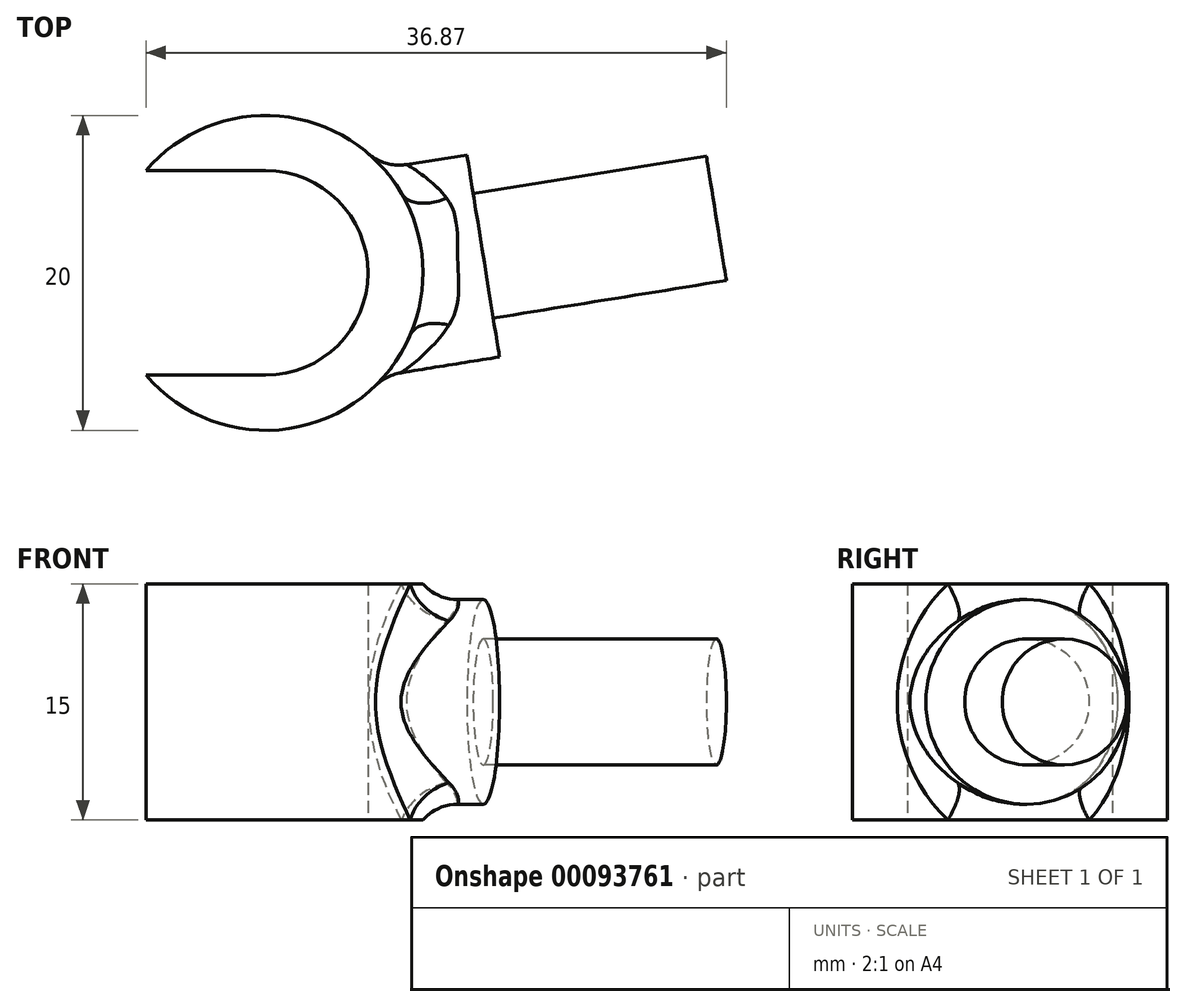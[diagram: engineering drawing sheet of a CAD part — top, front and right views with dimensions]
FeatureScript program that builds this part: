
annotation { "Feature Type Name" : "Feature", "Feature Type Description" : "" }
export const myFeature = defineFeature(function(context is Context, id is Id, definition is map)
    precondition{}
    {
        {
            var Q0;
            Q0=qCreatedBy(makeId("Top.planeOp"),FACE);
            var sketch = newSketch(context, id + "F0", { "sketchPlane" : qUnion([Q0])});
            skArc(sketch, "E0", {"start": v(-7.6, -6.5) * mm, "mid": v(10, 0) * mm, "end": v(-7.6, 6.5) * mm});
            skArc(sketch, "E1", {"start": v(0, -6.5) * mm, "mid": v(6.5, 0) * mm, "end": v(0, 6.5) * mm});
            skLineSegment(sketch, "E2", {"start": v(0, 6.5) * mm, "end": v(-7.6, 6.5) * mm});
            skLineSegment(sketch, "E3", {"start": v(0, -6.5) * mm, "end": v(-7.6, -6.5) * mm});
            skSolve(sketch);
        }
        {
            var Q0;
            Q0=makeQuery(id+"F0.imprint","IMPRINT",FACE,{"disambiguationData":[TD([[makeQuery(id+"F0.imprint","IMPRINT",EDGE,{"derivedFrom":sQuery(id+"F0.wireOp",EDGE,"E0")}),1.0]])]});
            extrude(context, id + "F1", {"entities" : qUnion([Q0]), "endBound" : BoundingType.SYMMETRIC, "depth" : 15 * mm});
        }
        {
            var Q0;
            Q0=qCreatedBy(makeId("Top.planeOp"),FACE);
            var sketch = newSketch(context, id + "F2", { "sketchPlane" : qUnion([Q0])});
            skLineSegment(sketch, "E4", {"start": v(7.1, 0) * mm, "end": v(28.63, 3.47) * mm});
            skLineSegment(sketch, "E5", {"start": v(28.63, 3.47) * mm, "end": v(29.27, -0.48) * mm});
            skLineSegment(sketch, "E6", {"start": v(29.27, -0.48) * mm, "end": v(14.46, -2.87) * mm});
            skLineSegment(sketch, "E7", {"start": v(14.46, -2.87) * mm, "end": v(14.86, -5.33) * mm});
            skLineSegment(sketch, "E8", {"start": v(14.86, -5.33) * mm, "end": v(5.48, -6.84) * mm});
            skLineSegment(sketch, "E9", {"start": v(5.48, -6.84) * mm, "end": v(7.1, 0) * mm});
            skSolve(sketch);
        }
        {
            var Q0;
            Q0=makeQuery(id+"F2.imprint","IMPRINT",FACE,{"disambiguationData":[TD([[makeQuery(id+"F2.imprint","IMPRINT",EDGE,{"derivedFrom":sQuery(id+"F2.wireOp",EDGE,"E4")}),-1.0]])]});
            var Q1;
            Q1=sQuery(id+"F2.wireOp",EDGE,"E4");
            revolve(context, id + "F3", {"operationType" : NewBodyOperationType.ADD, "entities" : qUnion([Q0]), "axis" : qUnion([Q1]), "revolveType" : RevolveType.FULL});
        }
        {
            var Q0;
            Q0=qCreatedBy(makeId("Top.planeOp"),FACE);
            var sketch = newSketch(context, id + "F4", { "sketchPlane" : qUnion([Q0])});
            skCircle(sketch, "E10", {"center": v(0, 0) * mm, "radius": 6.5 * mm});
            skSolve(sketch);
        }
        {
            var Q0;
            Q0=qSketchRegion(id+"F4",true);
            extrude(context, id + "F5", {"entities" : qUnion([Q0]), "operationType" : NewBodyOperationType.REMOVE, "endBound" : BoundingType.SYMMETRIC, "oppositeDirection" : true, "depth" : 25 * mm});
        }
        {
            var Q0;
            Q0=makeQuery(id+"F3.boolean.opBoolean","INTERSECT",EDGE,{"derivedFrom":[makeQuery(id+"F1.opExtrude","SWEPT_FACE",FACE,{"disambiguationData":[OSD([sQuery(id+"F0.wireOp",EDGE,"E0")])]}),makeQuery(id+"F3.opRevolve","SWEPT_FACE",FACE,{"disambiguationData":[OSD([sQuery(id+"F2.wireOp",EDGE,"E8")])]})]});
            fillet(context, id + "F6", {"entities" : qUnion([Q0]), "radius" : 3 * mm, "allowEdgeOverflow" : false});
        }
    });
